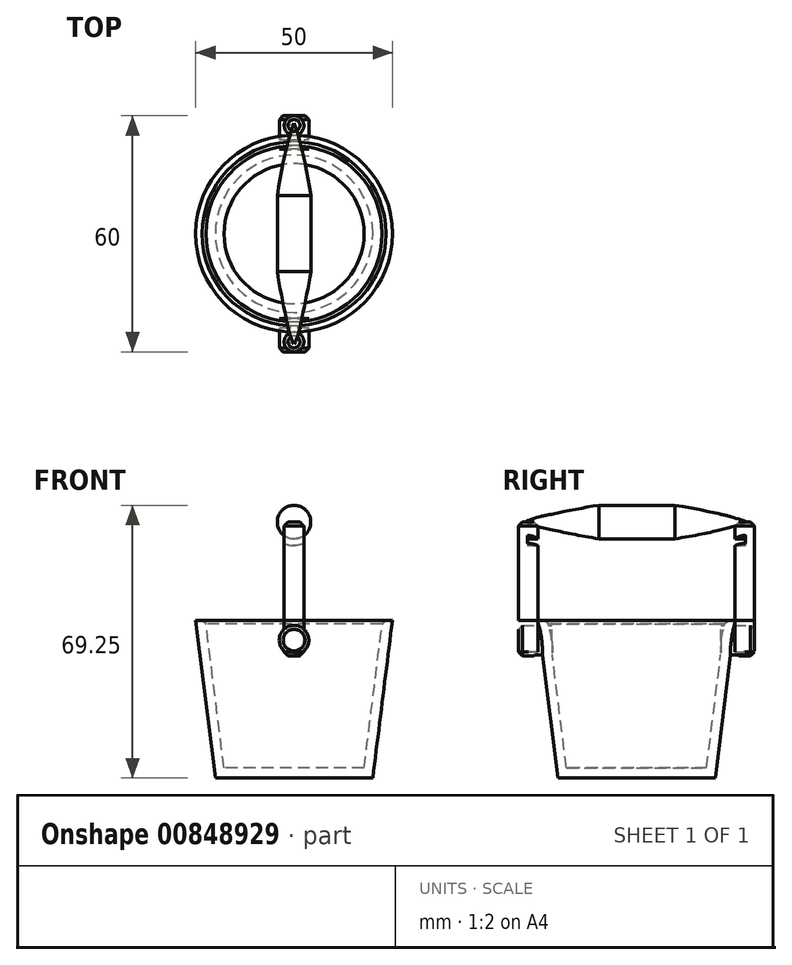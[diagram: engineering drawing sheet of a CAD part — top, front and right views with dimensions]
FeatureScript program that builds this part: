
annotation { "Feature Type Name" : "Feature", "Feature Type Description" : "" }
export const myFeature = defineFeature(function(context is Context, id is Id, definition is map)
    precondition{}
    {
        {
            var Q0;
            Q0=qCreatedBy(makeId("Top.planeOp"),FACE);
            var sketch = newSketch(context, id + "F0", { "sketchPlane" : qUnion([Q0])});
            skCircle(sketch, "E0", {"center": v(0, 0) * mm, "radius": 20 * mm});
            skSolve(sketch);
        }
        {
            var Q0;
            Q0=qCreatedBy(makeId("Top.planeOp"),FACE);
            cPlane(context, id + "F1", {"entities" : qUnion([Q0]), "cplaneType" : CPlaneType.OFFSET, "offset" : 40 * mm, "width" : 150 * mm, "height" : 150 * mm});
        }
        {
            var Q0;
            Q0=qCreatedBy(id+"F1.planeOp",FACE);
            var sketch = newSketch(context, id + "F2", { "sketchPlane" : qUnion([Q0])});
            skCircle(sketch, "E1", {"center": v(0, 0) * mm, "radius": 25 * mm});
            skSolve(sketch);
        }
        {
            var Q0;
            Q0=makeQuery(id+"F0.imprint","IMPRINT",FACE,{"disambiguationData":[TD([[makeQuery(id+"F0.imprint","IMPRINT",EDGE,{"derivedFrom":sQuery(id+"F0.wireOp",EDGE,"E0")}),1.0]])]});
            var Q1;
            Q1=makeQuery(id+"F2.imprint","IMPRINT",FACE,{"disambiguationData":[TD([[makeQuery(id+"F2.imprint","IMPRINT",EDGE,{"derivedFrom":sQuery(id+"F2.wireOp",EDGE,"E1")}),1.0]])]});
            loft(context, id + "F3", {"sheetProfilesArray" : [{ "sheetProfileEntities" : qUnion([Q0]) }, { "sheetProfileEntities" : qUnion([Q1]) }]});
        }
        {
            var Q0;
            Q0=makeQuery(id+"F3.opLoft","CAP_FACE",FACE,{"disambiguationData":[OSD([makeQuery(id+"F2.imprint","IMPRINT",FACE,{"disambiguationData":[TD([[makeQuery(id+"F2.imprint","IMPRINT",EDGE,{"derivedFrom":sQuery(id+"F2.wireOp",EDGE,"E1")}),1.0]])]})])],"isStart":true});
            shell(context, id + "F4", {"entities" : qUnion([Q0]), "thickness" : 2.5 * mm});
        }
        {
            var Q0;
            Q0=qCreatedBy(makeId("Front.planeOp"),FACE);
            var sketch = newSketch(context, id + "F5", { "sketchPlane" : qUnion([Q0])});
            skCircle(sketch, "E2", {"center": v(0, 35) * mm, "radius": 3.75 * mm});
            skSolve(sketch);
        }
        {
            var Q0;
            Q0=makeQuery(id+"F5.imprint","IMPRINT",FACE,{"disambiguationData":[TD([[makeQuery(id+"F5.imprint","IMPRINT",EDGE,{"derivedFrom":sQuery(id+"F5.wireOp",EDGE,"E2")}),1.0]])]});
            extrude(context, id + "F6", {"entities" : qUnion([Q0]), "operationType" : NewBodyOperationType.ADD, "endBound" : BoundingType.SYMMETRIC, "depth" : 60 * mm, "offsetDistance" : 25 * mm});
        }
        {
            var Q0;
            Q0=qCreatedBy(makeId("Front.planeOp"),FACE);
            var sketch = newSketch(context, id + "F7", { "sketchPlane" : qUnion([Q0])});
            skCircle(sketch, "E3", {"center": v(0, 35) * mm, "radius": 3.75 * mm});
            skSolve(sketch);
        }
        {
            var Q0;
            Q0 = qSketchRegion(id + "F7", true);
            extrude(context, id + "F8", {"entities" : qUnion([Q0]), "operationType" : NewBodyOperationType.REMOVE, "endBound" : BoundingType.SYMMETRIC, "oppositeDirection" : true, "depth" : 43 * mm, "offsetDistance" : 25 * mm});
        }
        {
            var Q0;
            Q0=qCreatedBy(id+"F1.planeOp",FACE);
            var sketch = newSketch(context, id + "F9", { "sketchPlane" : qUnion([Q0])});
            skCircle(sketch, "E4", {"center": v(0, 27.5) * mm, "radius": 2.5 * mm});
            skCircle(sketch, "E5", {"center": v(0, -27.5) * mm, "radius": 2.5 * mm});
            skSolve(sketch);
        }
        {
            var Q0;
            Q0 = qSketchRegion(id + "F9", true);
            extrude(context, id + "F10", {"entities" : qUnion([Q0]), "depth" : 25 * mm, "offsetDistance" : 25 * mm});
        }
        {
            var Q0;
            Q0=makeQuery(id+"F10.opExtrude","CAP_FACE",FACE,{"disambiguationData":[OSD([sQuery(id+"F9.wireOp",EDGE,"E4")])],"isStart":true});
            var Q1;
            Q1=makeQuery(id+"F10.opExtrude","CAP_FACE",FACE,{"disambiguationData":[OSD([sQuery(id+"F9.wireOp",EDGE,"E5")])],"isStart":true});
            extrude(context, id + "F11", {"entities" : qUnion([Q0, Q1]), "depth" : 9 * mm, "offsetDistance" : 25 * mm});
        }
        {
            var Q0;
            Q0=qCreatedBy(makeId("Right.planeOp"),FACE);
            var sketch = newSketch(context, id + "F12", { "sketchPlane" : qUnion([Q0])});
            skLineSegment(sketch, "E6", {"start": v(-28.06, 65) * mm, "end": v(28.06, 65) * mm});
            skFitSpline(sketch, "E7", {"points": [v(-28.06, 65) * mm, v(-20.38, 62.77) * mm, v(0, 60) * mm, v(20.38, 62.77) * mm, v(28.06, 65) * mm], "startDerivative": vector(30.2, -17.74) * mm, "endDerivative": vector(49.64, 18.1) * mm});
            skLineSegment(sketch, "E8", {"start": v(-28.06, 65) * mm, "end": v(42.92, 65) * mm, "construction": true});
            skSolve(sketch);
        }
        {
            var Q0;
            Q0=makeQuery(id+"F12.imprint","IMPRINT",FACE,{"disambiguationData":[TD([[makeQuery(id+"F12.imprint","IMPRINT",EDGE,{"derivedFrom":sQuery(id+"F12.wireOp",EDGE,"E6")}),-1.0]])]});
            var Q1;
            Q1=sQuery(id+"F12.wireOp",EDGE,"E8");
            revolve(context, id + "F13", {"surfaceOperationType" : NewSurfaceOperationType.NEW, "entities" : qUnion([Q0]), "axis" : qUnion([Q1]), "revolveType" : RevolveType.FULL});
        }
        {
            var Q0;
            Q0=qCreatedBy(makeId("Front.planeOp"),FACE);
            var sketch = newSketch(context, id + "F14", { "sketchPlane" : qUnion([Q0])});
            skCircle(sketch, "E9", {"center": v(0, 65) * mm, "radius": 4.25 * mm});
            skCircle(sketch, "E10", {"center": v(0, 65) * mm, "radius": 6 * mm});
            skSolve(sketch);
        }
        {
            var Q0;
            Q0 = qSketchRegion(id + "F14", true);
            extrude(context, id + "F15", {"entities" : qUnion([Q0]), "operationType" : NewBodyOperationType.REMOVE, "endBound" : BoundingType.SYMMETRIC, "depth" : 55.4 * mm, "offsetDistance" : 25 * mm});
        }
        {
            var Q0;
            Q0=makeQuery(id+"F10.opExtrude","CAP_EDGE",EDGE,{"disambiguationData":[OSD([sQuery(id+"F9.wireOp",EDGE,"E5")])],"isStart":false});
            var Q1;
            Q1=makeQuery(id+"F10.opExtrude","CAP_EDGE",EDGE,{"disambiguationData":[OSD([sQuery(id+"F9.wireOp",EDGE,"E4")])],"isStart":false});
            var Q2;
            Q2=makeQuery(id+"F6.opExtrude","CAP_EDGE",EDGE,{"disambiguationData":[OSD([sQuery(id+"F5.wireOp",EDGE,"E2")])],"isStart":false});
            var Q3;
            Q3=makeQuery(id+"F6.opExtrude","CAP_EDGE",EDGE,{"disambiguationData":[OSD([sQuery(id+"F5.wireOp",EDGE,"E2")])],"isStart":true});
            var Q4;
            Q4=makeQuery(id+"F11.opExtrude","CAP_EDGE",EDGE,{"disambiguationData":[OSD([sQuery(id+"F9.wireOp",EDGE,"E4")])],"isStart":false});
            var Q5;
            Q5=makeQuery(id+"F11.opExtrude","CAP_EDGE",EDGE,{"disambiguationData":[OSD([sQuery(id+"F9.wireOp",EDGE,"E5")])],"isStart":false});
            var Q6;
            Q6=makeQuery(id+"F4.opShell","OFFSET_EDGE",EDGE,{"disambiguationData":[OSD([sQuery(id+"F2.wireOp",EDGE,"E1")])]});
            chamfer(context, id + "F16", {"entities" : qUnion([Q0, Q1, Q2, Q3, Q4, Q5, Q6]), "width" : 1 * mm, "tangentPropagation" : true});
        }
    });
